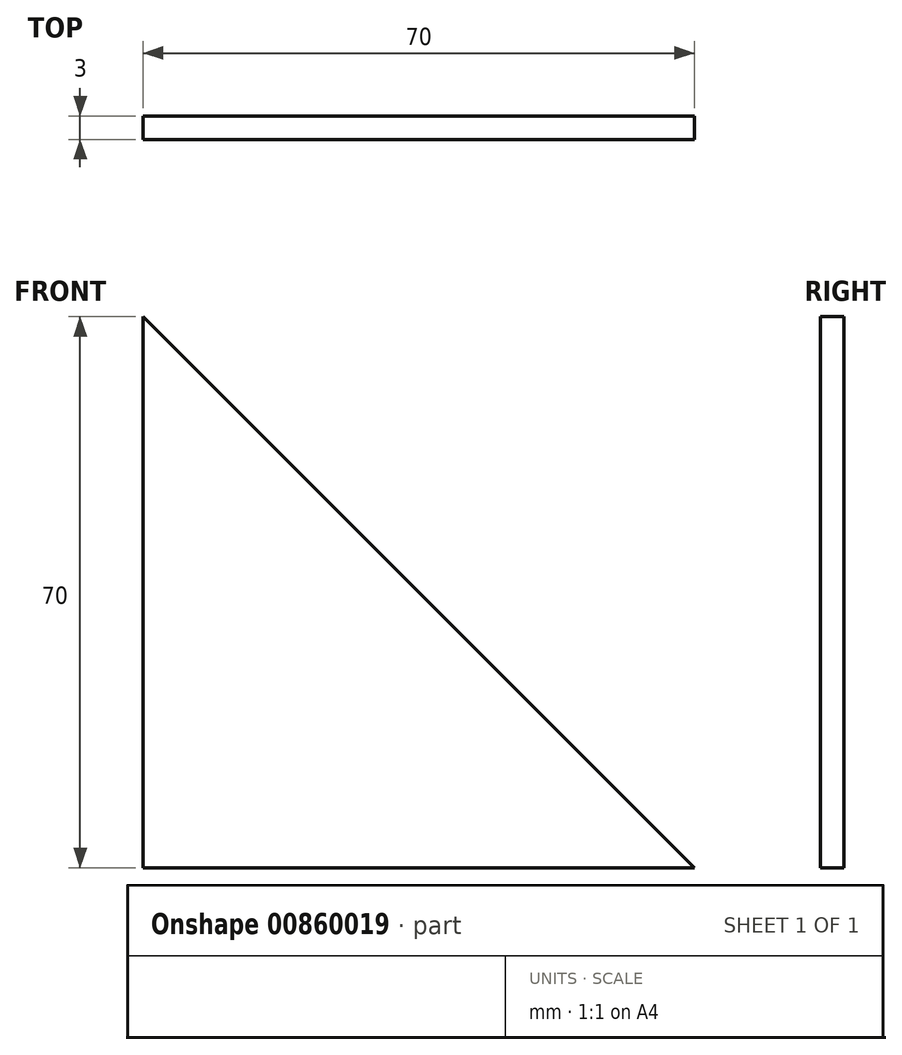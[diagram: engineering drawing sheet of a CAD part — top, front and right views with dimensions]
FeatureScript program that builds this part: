
annotation { "Feature Type Name" : "Feature", "Feature Type Description" : "" }
export const myFeature = defineFeature(function(context is Context, id is Id, definition is map)
    precondition{}
    {
        {
            var Q0;
            Q0=qCreatedBy(makeId("Front.planeOp"),FACE);
            var sketch = newSketch(context, id + "F0", { "sketchPlane" : qUnion([Q0])});
            skLineSegment(sketch, "E0", {"start": v(0, 0) * mm, "end": v(0, 70) * mm});
            skLineSegment(sketch, "E1", {"start": v(0, 0) * mm, "end": v(70, 0) * mm});
            skLineSegment(sketch, "E2", {"start": v(0, 70) * mm, "end": v(70, 0) * mm});
            skSolve(sketch);
        }
        {
            var Q0;
            Q0 = qSketchRegion(id + "F0", true);
            extrude(context, id + "F1", {"entities" : qUnion([Q0]), "endBound" : BoundingType.SYMMETRIC, "depth" : 3 * mm, "offsetDistance" : 25 * mm});
        }
    });
